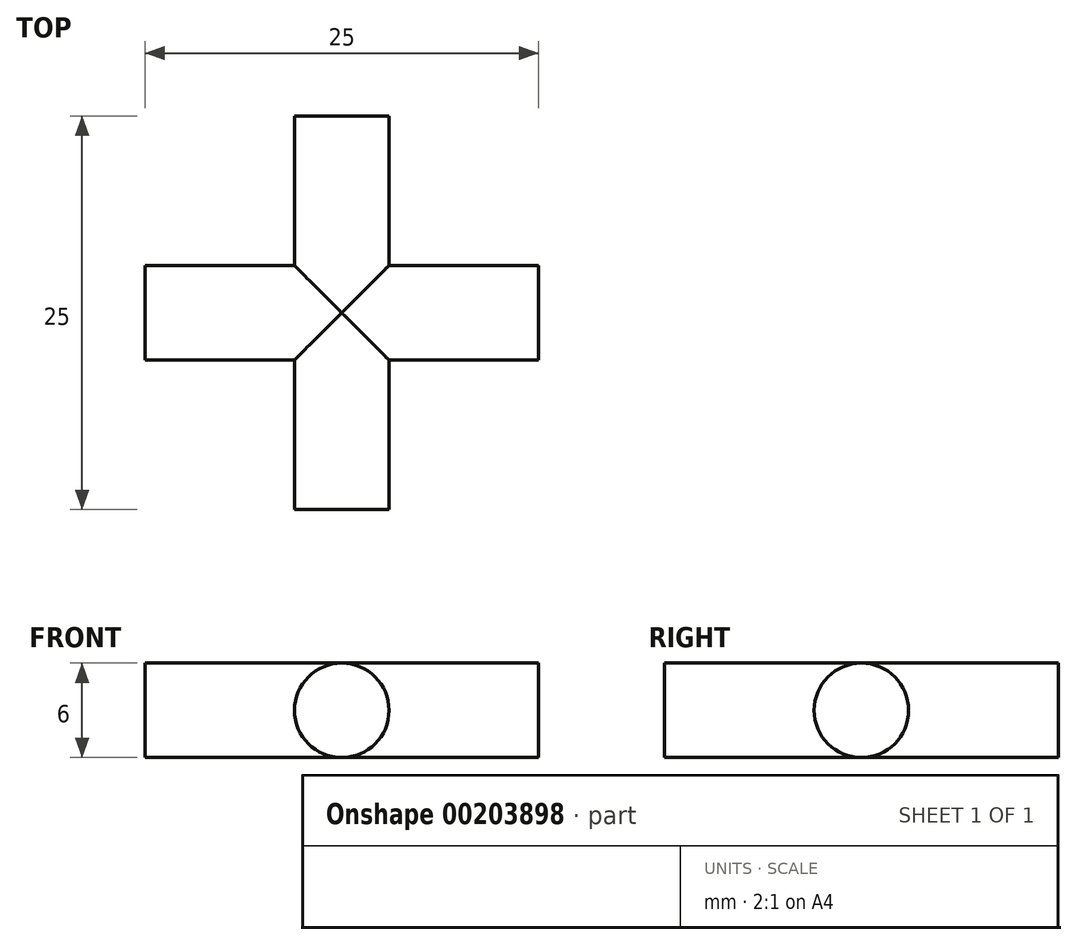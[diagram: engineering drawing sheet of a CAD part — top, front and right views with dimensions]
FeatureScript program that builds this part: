
annotation { "Feature Type Name" : "Feature", "Feature Type Description" : "" }
export const myFeature = defineFeature(function(context is Context, id is Id, definition is map)
    precondition{}
    {
        {
            var Q0;
            Q0=qCreatedBy(makeId("Right.planeOp"),FACE);
            var sketch = newSketch(context, id + "F0", { "sketchPlane" : qUnion([Q0])});
            skCircle(sketch, "E0", {"center": v(0, 0) * mm, "radius": 3 * mm});
            skSolve(sketch);
        }
        {
            var Q0;
            Q0=makeQuery(id+"F0.imprint","IMPRINT",FACE,{"disambiguationData":[TD([[makeQuery(id+"F0.imprint","IMPRINT",EDGE,{"derivedFrom":sQuery(id+"F0.wireOp",EDGE,"E0")}),1.0]])]});
            extrude(context, id + "F1", {"entities" : qUnion([Q0]), "depth" : 12.5 * mm, "hasSecondDirection" : true, "secondDirectionOppositeDirection" : true, "secondDirectionDepth" : 12.5 * mm});
        }
        {
            var Q0;
            Q0=qCreatedBy(makeId("Front.planeOp"),FACE);
            var sketch = newSketch(context, id + "F2", { "sketchPlane" : qUnion([Q0])});
            skCircle(sketch, "E1", {"center": v(0, 0) * mm, "radius": 3 * mm});
            skSolve(sketch);
        }
        {
            var Q0;
            Q0 = qSketchRegion(id + "F2", true);
            extrude(context, id + "F3", {"entities" : qUnion([Q0]), "operationType" : NewBodyOperationType.ADD, "depth" : 12.5 * mm, "hasSecondDirection" : true, "secondDirectionOppositeDirection" : true, "secondDirectionDepth" : 12.5 * mm});
        }
    });
